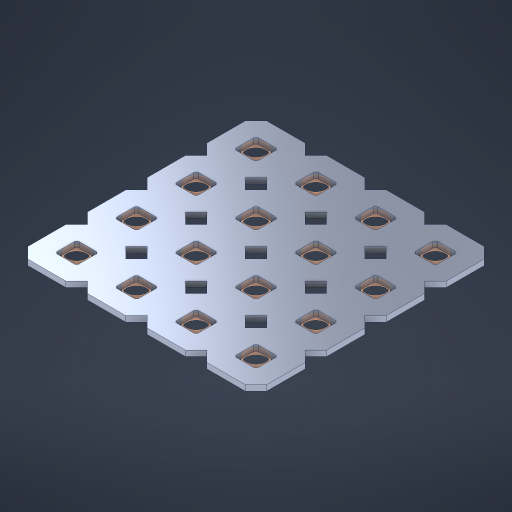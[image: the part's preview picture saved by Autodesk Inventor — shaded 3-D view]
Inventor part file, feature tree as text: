
AUTODESK INVENTOR PART (.ipt)
format: ipt  version: 2023 (Build 270158000, 158)  size: 441,856 bytes
history: native  units: in
note: dims shown in document units (in); Inventor stores cm internally (conversion verified against a paired STEP export)
features: other x17, extrude x15, sketch x2, pattern_linear x1
ambient origin geometry x8: Origin, YZ Plane, XZ Plane, XY Plane, X Axis, Y Axis, Z Axis, Center Point
bodies: Solid1 (feature_tree), Body (feature_tree)
feature tree (35):
  pattern_linear  "Rectangular Pattern1"  Spacing1=0.09in  [1 undecoded]
  sketch  "Sketch1"  dims[d1=0.5in]
  sketch  "Sketch2"  dims[d2=0.182in d3=0.09in d4=0.09in d5=0.09in d6=0.09in d7=0.09in d8=0.09in d9=0.09in d10=0.09in d11=0.02in d13=0.0in d14=0.172in d15=0.0625in d16=0.0in d19=0.5in d22=0.5in]
  other  "Srf1"
  other  "Srf126"
  other  "Srf127"
  other  "Srf128"
  other  "Srf268"
  other  "Srf269"
  other  "Srf270"
  other  "Srf271"
  other  "Srf293"
  other  "Srf294"
  other  "Srf295"
  other  "Srf296"
  other  "Srf318"
  other  "Srf319"
  other  "Srf320"
  other  "Srf321"
  other  "Circle"
  extrude  "ExtrusionSrf126"  Depth=0.09in
  extrude  "ExtrusionSrf127"  Depth=0.09in
  extrude  "ExtrusionSrf128"  Depth=0.09in
  extrude  "ExtrusionSrf268"  Depth=0.09in
  extrude  "ExtrusionSrf269"  Depth=0.09in
  extrude  "ExtrusionSrf270"  Depth=0.09in
  extrude  "ExtrusionSrf271"  Depth=0.09in
  extrude  "ExtrusionSrf293"  Depth=0.02in
  extrude  "ExtrusionSrf294"  TaperAngle=0.0deg  [1 undecoded]
  extrude  "ExtrusionSrf295"  Depth=0.5in
  extrude  "ExtrusionSrf296"  Depth=0.5in TaperAngle=0.0deg
  extrude  "ExtrusionSrf318"  Depth=0.5in
  extrude  "ExtrusionSrf319"  Depth=0.5in
  extrude  "ExtrusionSrf320"  [1 undecoded]
  extrude  "ExtrusionSrf321"  [1 undecoded]
note: 4 required parameter values undecoded (feature->parameter linkage not recoverable at this tier; creation-order binding heuristic only, values carry confidence <= 0.55)
